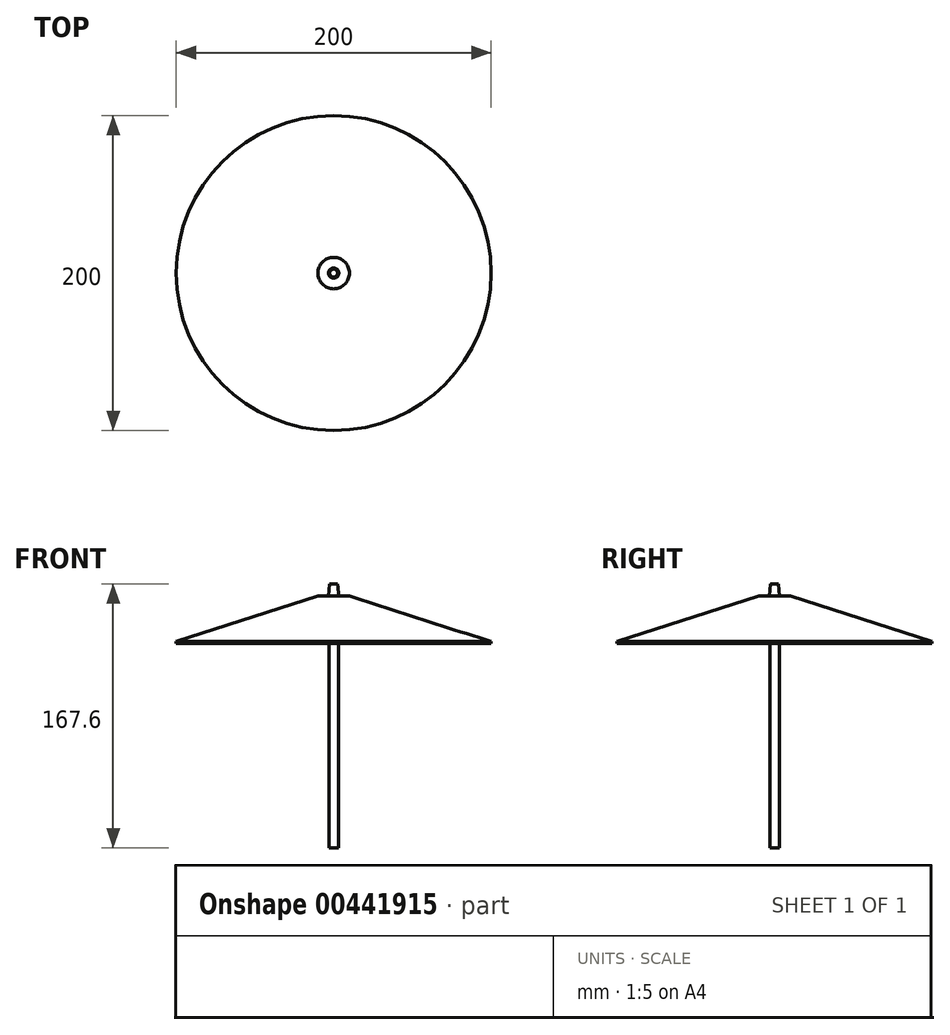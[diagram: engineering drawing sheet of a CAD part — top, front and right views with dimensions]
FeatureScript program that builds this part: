
annotation { "Feature Type Name" : "Feature", "Feature Type Description" : "" }
export const myFeature = defineFeature(function(context is Context, id is Id, definition is map)
    precondition{}
    {
        {
            var Q0;
            Q0=qCreatedBy(makeId("Top.planeOp"),FACE);
            var sketch = newSketch(context, id + "F0", { "sketchPlane" : qUnion([Q0])});
            skCircle(sketch, "E0", {"center": v(0, 0) * mm, "radius": 3 * mm});
            skSolve(sketch);
        }
        {
            var Q0;
            Q0=makeQuery(id+"F0.imprint","IMPRINT",FACE,{"disambiguationData":[TD([[makeQuery(id+"F0.imprint","IMPRINT",EDGE,{"derivedFrom":sQuery(id+"F0.wireOp",EDGE,"E0")}),1.0]])]});
            extrude(context, id + "F1", {"entities" : qUnion([Q0]), "depth" : 130 * mm});
        }
        {
            var Q0;
            Q0=makeQuery(id+"F1.opExtrude","CAP_FACE",FACE,{"disambiguationData":[OSD([sQuery(id+"F0.wireOp",EDGE,"E0")])],"isStart":false});
            var sketch = newSketch(context, id + "F2", { "sketchPlane" : qUnion([Q0])});
            skCircle(sketch, "E1", {"center": v(0, 0) * mm, "radius": 100 * mm});
            skSolve(sketch);
        }
        {
            var Q0;
            Q0=makeQuery(id+"F2.imprint","IMPRINT",FACE,{"disambiguationData":[TD([[makeQuery(id+"F2.imprint","IMPRINT",EDGE,{"derivedFrom":sQuery(id+"F2.wireOp",EDGE,"E1")}),1.0]])]});
            var Q1;
            Q1=makeQuery(id+"F2.imprint","IMPRINT",FACE,{"disambiguationData":[TD([[makeQuery(id+"F2.imprint","IMPRINT",EDGE,{"derivedFrom":makeQuery(id+"F1.opExtrude","CAP_EDGE",EDGE,{"disambiguationData":[OSD([sQuery(id+"F0.wireOp",EDGE,"E0")])],"isStart":false})}),1.0]])]});
            extrude(context, id + "F3", {"entities" : qUnion([Q0, Q1]), "operationType" : NewBodyOperationType.ADD, "depth" : 30 * mm});
        }
        {
            var Q0;
            Q0=makeQuery(id+"F3.opExtrude","CAP_EDGE",EDGE,{"disambiguationData":[OSD([sQuery(id+"F2.wireOp",EDGE,"E1")])],"isStart":false});
            chamfer(context, id + "F4", {"entities" : qUnion([Q0]), "chamferType" : ChamferType.TWO_OFFSETS, "width1" : 90 * mm, "oppositeDirection" : false, "width2" : 29 * mm, "tangentPropagation" : true});
        }
        {
            var Q0;
            Q0=makeQuery(id+"F3.opExtrude","CAP_FACE",FACE,{"disambiguationData":[OSD([sQuery(id+"F2.wireOp",EDGE,"E1")])],"isStart":false});
            var sketch = newSketch(context, id + "F5", { "sketchPlane" : qUnion([Q0])});
            skCircle(sketch, "E2", {"center": v(0, 0) * mm, "radius": 3.5 * mm});
            skSolve(sketch);
        }
        {
            var Q0;
            Q0=makeQuery(id+"F5.imprint","IMPRINT",FACE,{"disambiguationData":[TD([[makeQuery(id+"F5.imprint","IMPRINT",EDGE,{"derivedFrom":sQuery(id+"F5.wireOp",EDGE,"E2")}),1.0]])]});
            extrude(context, id + "F6", {"entities" : qUnion([Q0]), "operationType" : NewBodyOperationType.ADD, "depth" : 7.6 * mm});
        }
        {
            var Q0;
            Q0=makeQuery(id+"F6.opExtrude","CAP_EDGE",EDGE,{"disambiguationData":[OSD([sQuery(id+"F5.wireOp",EDGE,"E2")])],"isStart":false});
            chamfer(context, id + "F7", {"entities" : qUnion([Q0]), "chamferType" : ChamferType.TWO_OFFSETS, "width1" : 1 * mm, "oppositeDirection" : false, "width2" : 10 * mm, "tangentPropagation" : true});
        }
    });
